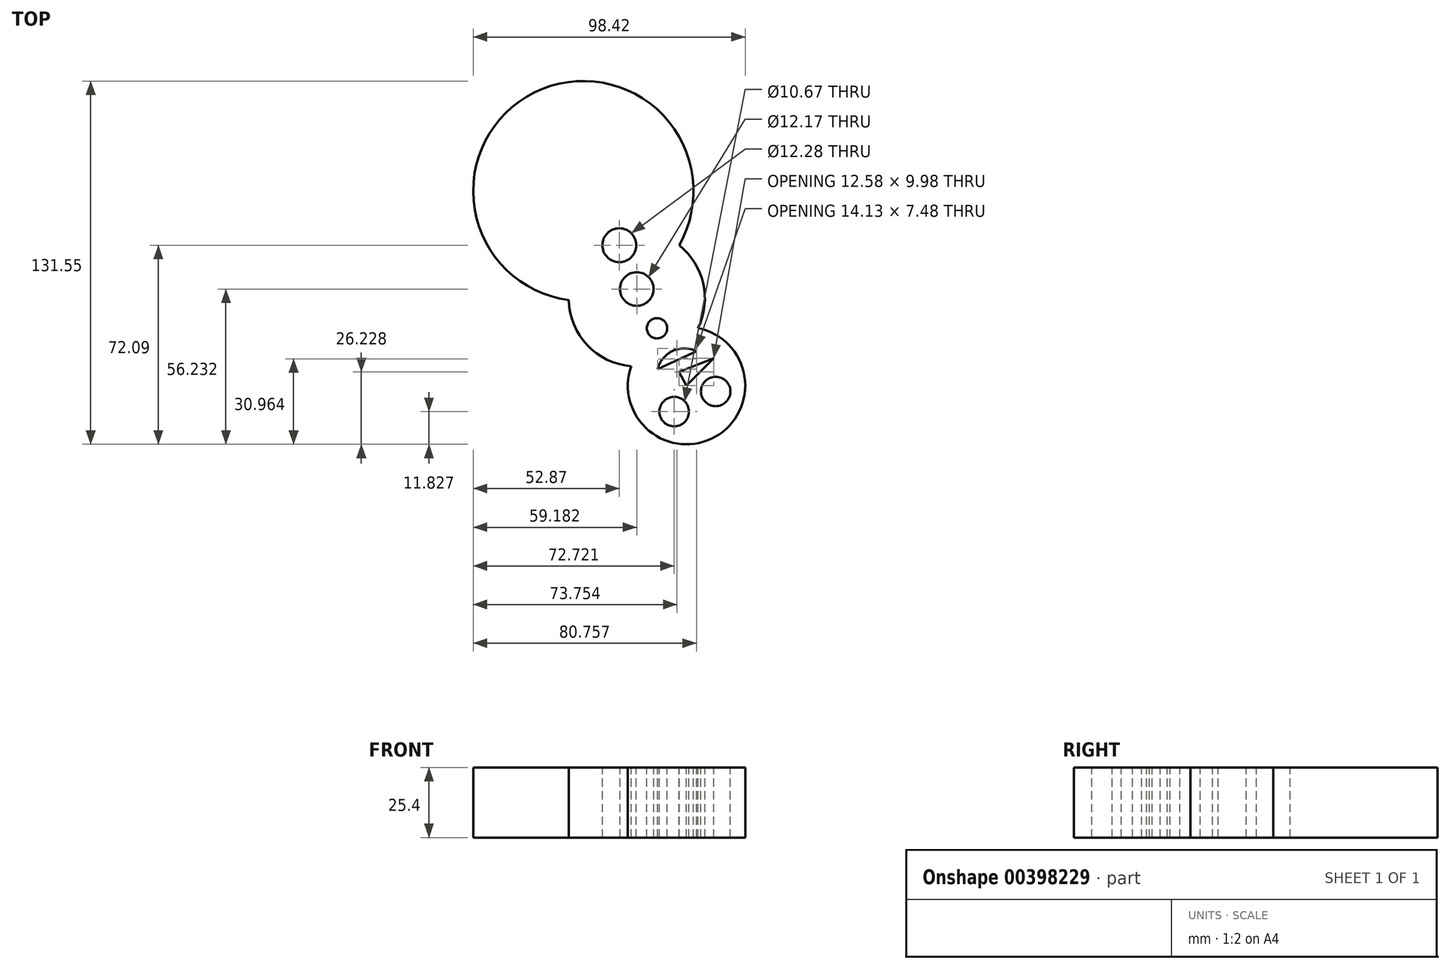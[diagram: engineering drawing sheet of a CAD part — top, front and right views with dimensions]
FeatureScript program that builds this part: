
annotation { "Feature Type Name" : "Feature", "Feature Type Description" : "" }
export const myFeature = defineFeature(function(context is Context, id is Id, definition is map)
    precondition{}
    {
        {
            var Q0;
            Q0=qCreatedBy(makeId("Top.planeOp"),FACE);
            var sketch = newSketch(context, id + "F0", { "sketchPlane" : qUnion([Q0])});
            skArc(sketch, "E0", {"start": v(34.7, 0) * mm, "mid": v(-17.75, 55.29) * mm, "end": v(-5.3, -19.9) * mm});
            skPoint(sketch, "E1.right.end.orphan", {"position": v(0, 25.09) * mm});
            skArc(sketch, "E2", {"start": v(-5.3, -19.9) * mm, "mid": v(1.42, -36.18) * mm, "end": v(17.3, -43.81) * mm});
            skPoint(sketch, "E3.top.end.orphan", {"position": v(0, -30.08) * mm});
            skArc(sketch, "E4", {"start": v(17.3, -43.81) * mm, "mid": v(47.84, -69.3) * mm, "end": v(41.5, -30.03) * mm});
            skArc(sketch, "E5.trimOffspring", {"start": v(41.5, -30.03) * mm, "mid": v(43.36, -13.82) * mm, "end": v(34.7, 0) * mm});
            skCircle(sketch, "E6", {"center": v(47.88, -52.95) * mm, "radius": 5.33 * mm});
            skCircle(sketch, "E7", {"center": v(32.87, -60.26) * mm, "radius": 5.33 * mm});
            skLineSegment(sketch, "E8", {"start": v(37.33, -50.85) * mm, "end": v(47.2, -40.88) * mm});
            skLineSegment(sketch, "E9", {"start": v(37.33, -50.85) * mm, "end": v(34.62, -45.86) * mm});
            skPoint(sketch, "E9.endSnap0", {"position": v(42.26, -45.86) * mm});
            skLineSegment(sketch, "E10", {"start": v(34.62, -45.86) * mm, "end": v(47.2, -40.88) * mm});
            skArc(sketch, "E11", {"start": v(40.97, -38.4) * mm, "mid": v(32.38, -38.3) * mm, "end": v(26.84, -44.87) * mm});
            skLineSegment(sketch, "E12", {"start": v(40.97, -38.4) * mm, "end": v(26.84, -44.87) * mm});
            skCircle(sketch, "E13", {"center": v(26.65, -30.08) * mm, "radius": 3.68 * mm});
            skCircle(sketch, "E14", {"center": v(19.33, -15.86) * mm, "radius": 6.09 * mm});
            skCircle(sketch, "E15", {"center": v(13.02, 0) * mm, "radius": 6.14 * mm});
            skLineSegment(sketch, "E16", {"start": v(37.85, -50.32) * mm, "end": v(35.35, -45.57) * mm});
            skPoint(sketch, "E17.orphan", {"position": v(-17.75, 55.29) * mm});
            skPoint(sketch, "E18.orphan", {"position": v(47.84, -69.3) * mm});
            skSolve(sketch);
        }
        {
            var Q0;
            Q0 = qSketchRegion(id + "F0", true);
            extrude(context, id + "F1", {"entities" : qUnion([Q0]), "oppositeDirection" : true, "depth" : 25.4 * mm});
        }
    });
